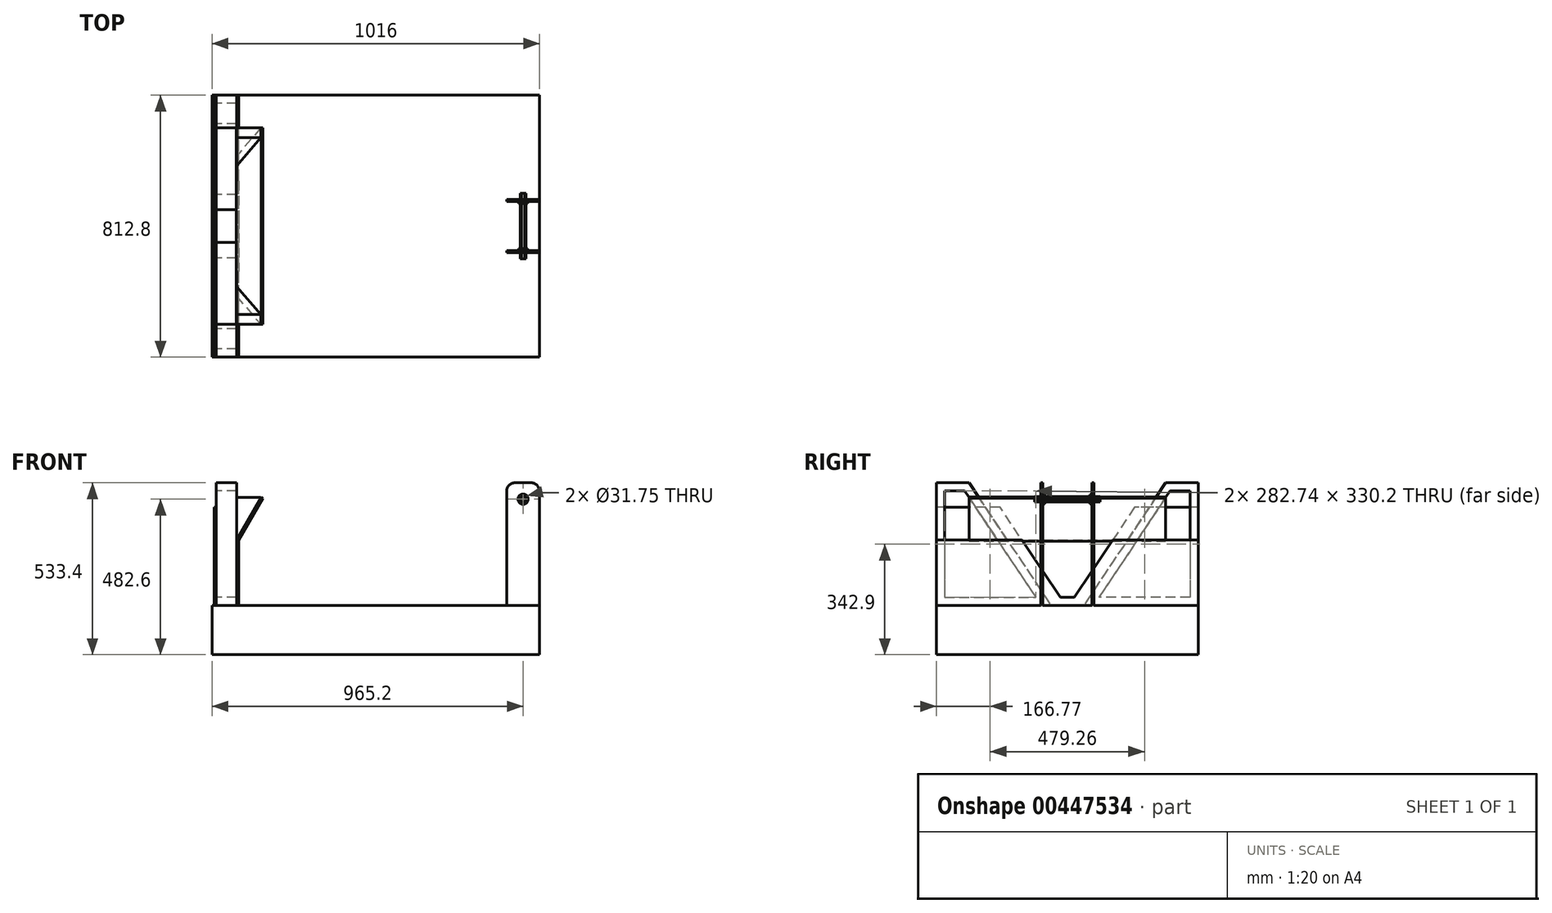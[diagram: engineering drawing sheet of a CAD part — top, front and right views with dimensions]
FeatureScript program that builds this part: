
annotation { "Feature Type Name" : "Feature", "Feature Type Description" : "" }
export const myFeature = defineFeature(function(context is Context, id is Id, definition is map)
    precondition{}
    {
        {
            var Q0;
            Q0=qCreatedBy(makeId("Top.planeOp"),FACE);
            cPlane(context, id + "F0", {"entities" : qUnion([Q0]), "cplaneType" : CPlaneType.OFFSET, "offset" : 76.2 * mm, "width" : 152.4 * mm, "height" : 152.4 * mm});
        }
        {
            var Q0;
            Q0=qCreatedBy(id+"F0.planeOp",FACE);
            var sketch = newSketch(context, id + "F1", { "sketchPlane" : qUnion([Q0])});
            skLineSegment(sketch, "E0.bottom", {"start": v(508, -406.4) * mm, "end": v(-508, -406.4) * mm});
            skLineSegment(sketch, "E0.top", {"start": v(508, 406.4) * mm, "end": v(-508, 406.4) * mm});
            skLineSegment(sketch, "E0.left", {"start": v(508, -406.4) * mm, "end": v(508, 406.4) * mm});
            skLineSegment(sketch, "E0.right", {"start": v(-508, -406.4) * mm, "end": v(-508, 406.4) * mm});
            skPoint(sketch, "E0.middle", {"position": v(0, 0) * mm});
            skSolve(sketch);
        }
        {
            var Q0;
            Q0 = qSketchRegion(id + "F1", true);
            extrude(context, id + "F2", {"entities" : qUnion([Q0]), "depth" : 152.4 * mm});
        }
        {
            var Q0;
            Q0=makeQuery(id+"F2.opExtrude","SWEPT_FACE",FACE,{"disambiguationData":[OSD([sQuery(id+"F1.wireOp",EDGE,"E0.right")])]});
            cPlane(context, id + "F3", {"entities" : qUnion([Q0]), "cplaneType" : CPlaneType.OFFSET, "offset" : 12.7 * mm, "oppositeDirection" : true, "width" : 152.4 * mm, "height" : 152.4 * mm});
        }
        {
            var Q0;
            Q0=qCreatedBy(id+"F3.planeOp",FACE);
            var sketch = newSketch(context, id + "F4", { "sketchPlane" : qUnion([Q0])});
            skLineSegment(sketch, "E1", {"start": v(-406.4, 609.6) * mm, "end": v(-406.4, 228.6) * mm});
            skLineSegment(sketch, "E2", {"start": v(-406.4, 228.6) * mm, "end": v(-50.8, 228.6) * mm});
            skLineSegment(sketch, "E3", {"start": v(0, 0) * mm, "end": v(-770.92, 0) * mm, "construction": true});
            skLineSegment(sketch, "E4", {"start": v(0, 0) * mm, "end": v(0, 808.5) * mm, "construction": true});
            skPoint(sketch, "E4.endSnap0", {"position": v(0, 228.6) * mm});
            skCircle(sketch, "E5", {"center": v(0, 404.25) * mm, "radius": 139.7 * mm, "construction": true});
            skLineSegment(sketch, "E6", {"start": v(-406.4, 609.6) * mm, "end": v(-304.8, 609.6) * mm});
            skLineSegment(sketch, "E7", {"start": v(-304.8, 609.6) * mm, "end": v(-50.8, 228.6) * mm});
            skLineSegment(sketch, "E8", {"start": v(-527.33, 330.2) * mm, "end": v(421.98, 330.2) * mm, "construction": true});
            skCircle(sketch, "E9", {"center": v(0, 404.25) * mm, "radius": 9.52 * mm, "construction": true});
            skLineSegment(sketch, "E10.MirrorCS", {"start": v(304.8, 609.6) * mm, "end": v(50.8, 228.6) * mm});
            skLineSegment(sketch, "E11.MirrorCS", {"start": v(406.4, 609.6) * mm, "end": v(304.8, 609.6) * mm});
            skLineSegment(sketch, "E12.MirrorCS", {"start": v(406.4, 609.6) * mm, "end": v(406.4, 228.6) * mm});
            skLineSegment(sketch, "E13.MirrorCS", {"start": v(406.4, 228.6) * mm, "end": v(50.8, 228.6) * mm});
            skLineSegment(sketch, "E14.0", {"start": v(-318.4, 584.2) * mm, "end": v(-98.26, 254) * mm});
            skLineSegment(sketch, "E14.1", {"start": v(-381, 584.2) * mm, "end": v(-318.4, 584.2) * mm});
            skLineSegment(sketch, "E14.2", {"start": v(-381, 584.2) * mm, "end": v(-381, 254) * mm});
            skLineSegment(sketch, "E14.3", {"start": v(-381, 254) * mm, "end": v(-98.26, 254) * mm});
            skLineSegment(sketch, "E15.0", {"start": v(318.4, 584.2) * mm, "end": v(98.26, 254) * mm});
            skLineSegment(sketch, "E15.1", {"start": v(381, 584.2) * mm, "end": v(318.4, 584.2) * mm});
            skLineSegment(sketch, "E15.2", {"start": v(381, 584.2) * mm, "end": v(381, 254) * mm});
            skLineSegment(sketch, "E15.3", {"start": v(381, 254) * mm, "end": v(98.26, 254) * mm});
            skSolve(sketch);
        }
        {
            var Q0;
            Q0=makeQuery(id+"F4.imprint","IMPRINT",FACE,{"disambiguationData":[TD([[makeQuery(id+"F4.imprint","IMPRINT",EDGE,{"derivedFrom":sQuery(id+"F4.wireOp",EDGE,"E1")}),1.0]])]});
            var Q1;
            Q1=makeQuery(id+"F4.imprint","IMPRINT",FACE,{"disambiguationData":[TD([[makeQuery(id+"F4.imprint","IMPRINT",EDGE,{"derivedFrom":sQuery(id+"F4.wireOp",EDGE,"E10.MirrorCS")}),1.0]])]});
            extrude(context, id + "F5", {"entities" : qUnion([Q0, Q1]), "oppositeDirection" : true, "depth" : 63.5 * mm});
        }
        {
            var Q0;
            Q0=makeQuery(id+"F5.opExtrude","CAP_FACE",FACE,{"disambiguationData":[OSD([sQuery(id+"F4.wireOp",EDGE,"E1"),sQuery(id+"F4.wireOp",EDGE,"E2"),sQuery(id+"F4.wireOp",EDGE,"E6"),sQuery(id+"F4.wireOp",EDGE,"E7"),sQuery(id+"F4.wireOp",EDGE,"E14.0"),sQuery(id+"F4.wireOp",EDGE,"E14.1"),sQuery(id+"F4.wireOp",EDGE,"E14.2"),sQuery(id+"F4.wireOp",EDGE,"E14.3")])],"isStart":true});
            var sketch = newSketch(context, id + "F6", { "sketchPlane" : qUnion([Q0])});
            skLineSegment(sketch, "E16.0", {"start": v(-406.4, 533.4) * mm, "end": v(-406.4, 228.6) * mm});
            skLineSegment(sketch, "E17.0", {"start": v(406.4, 533.4) * mm, "end": v(406.4, 228.6) * mm});
            skLineSegment(sketch, "E18", {"start": v(-406.4, 533.4) * mm, "end": v(-208.2, 533.4) * mm});
            skLineSegment(sketch, "E19", {"start": v(-208.2, 533.4) * mm, "end": v(-21.94, 254) * mm});
            skLineSegment(sketch, "E20", {"start": v(-21.94, 254) * mm, "end": v(21.94, 254) * mm});
            skLineSegment(sketch, "E21", {"start": v(21.94, 254) * mm, "end": v(208.2, 533.4) * mm});
            skLineSegment(sketch, "E22", {"start": v(208.2, 533.4) * mm, "end": v(406.4, 533.4) * mm});
            skLineSegment(sketch, "E23", {"start": v(-406.4, 228.6) * mm, "end": v(406.4, 228.6) * mm});
            skPoint(sketch, "E24.orphan", {"position": v(-406.4, 609.6) * mm});
            skPoint(sketch, "E25.orphan", {"position": v(406.4, 609.6) * mm});
            skSolve(sketch);
        }
        {
            var Q0;
            Q0 = qSketchRegion(id + "F6", true);
            extrude(context, id + "F7", {"entities" : qUnion([Q0]), "depth" : 6.35 * mm});
        }
        {
            var Q0;
            Q0=makeQuery(id+"F5.opExtrude","CAP_FACE",FACE,{"disambiguationData":[OSD([sQuery(id+"F4.wireOp",EDGE,"E1"),sQuery(id+"F4.wireOp",EDGE,"E2"),sQuery(id+"F4.wireOp",EDGE,"E6"),sQuery(id+"F4.wireOp",EDGE,"E7"),sQuery(id+"F4.wireOp",EDGE,"E14.0"),sQuery(id+"F4.wireOp",EDGE,"E14.1"),sQuery(id+"F4.wireOp",EDGE,"E14.2"),sQuery(id+"F4.wireOp",EDGE,"E14.3")])],"isStart":false});
            var sketch = newSketch(context, id + "F8", { "sketchPlane" : qUnion([Q0])});
            skLineSegment(sketch, "E26.0", {"start": v(-21.94, 254) * mm, "end": v(-140.48, 431.8) * mm});
            skLineSegment(sketch, "E27.0", {"start": v(140.48, 431.8) * mm, "end": v(21.94, 254) * mm});
            skLineSegment(sketch, "E28.0", {"start": v(406.4, 431.8) * mm, "end": v(406.4, 228.6) * mm});
            skLineSegment(sketch, "E29.0", {"start": v(-406.4, 228.6) * mm, "end": v(406.4, 228.6) * mm});
            skLineSegment(sketch, "E30.0", {"start": v(-406.4, 431.8) * mm, "end": v(-406.4, 228.6) * mm});
            skPoint(sketch, "E31.orphan", {"position": v(-406.4, 609.6) * mm});
            skPoint(sketch, "E32.orphan", {"position": v(406.4, 609.6) * mm});
            skLineSegment(sketch, "E33.0", {"start": v(21.94, 254) * mm, "end": v(-21.94, 254) * mm});
            skLineSegment(sketch, "E34", {"start": v(-406.4, 431.8) * mm, "end": v(-140.48, 431.8) * mm});
            skLineSegment(sketch, "E35.trimOffspring", {"start": v(140.48, 431.8) * mm, "end": v(406.4, 431.8) * mm});
            skPoint(sketch, "E36.0.start.orphan", {"position": v(-208.2, 533.4) * mm});
            skPoint(sketch, "E37.0.end.orphan", {"position": v(208.2, 533.4) * mm});
            skPoint(sketch, "E38.orphan", {"position": v(406.4, 533.4) * mm});
            skPoint(sketch, "E39.orphan", {"position": v(-406.4, 533.4) * mm});
            skSolve(sketch);
        }
        {
            var Q0;
            Q0 = qSketchRegion(id + "F8", true);
            extrude(context, id + "F9", {"entities" : qUnion([Q0]), "depth" : 6.35 * mm});
        }
        {
            var Q0;
            Q0=makeQuery(id+"F9.opExtrude","CAP_EDGE",EDGE,{"disambiguationData":[OSD([sQuery(id+"F8.wireOp",EDGE,"E35.trimOffspring")])],"isStart":false});
            var Q1;
            Q1=makeQuery(id+"F5.opExtrude","CAP_FACE",FACE,{"disambiguationData":[OSD([sQuery(id+"F4.wireOp",EDGE,"E1"),sQuery(id+"F4.wireOp",EDGE,"E2"),sQuery(id+"F4.wireOp",EDGE,"E6"),sQuery(id+"F4.wireOp",EDGE,"E7"),sQuery(id+"F4.wireOp",EDGE,"E14.0"),sQuery(id+"F4.wireOp",EDGE,"E14.1"),sQuery(id+"F4.wireOp",EDGE,"E14.2"),sQuery(id+"F4.wireOp",EDGE,"E14.3")])],"isStart":false});
            cPlane(context, id + "F10", {"entities" : qUnion([Q0, Q1]), "cplaneType" : CPlaneType.LINE_ANGLE, "offset" : 25.4 * mm, "angle" : 30 * degree, "width" : 152.4 * mm, "height" : 152.4 * mm});
        }
        {
            var Q0;
            Q0=qCreatedBy(id+"F10.planeOp",FACE);
            var sketch = newSketch(context, id + "F11", { "sketchPlane" : qUnion([Q0])});
            skLineSegment(sketch, "E40.bottom", {"start": v(304.8, 312.03) * mm, "end": v(-304.8, 312.03) * mm});
            skLineSegment(sketch, "E40.top", {"start": v(304.8, 158.05) * mm, "end": v(-304.8, 158.05) * mm});
            skLineSegment(sketch, "E40.left", {"start": v(304.8, 312.03) * mm, "end": v(304.8, 158.05) * mm});
            skLineSegment(sketch, "E40.right", {"start": v(-304.8, 312.03) * mm, "end": v(-304.8, 158.05) * mm});
            skSolve(sketch);
        }
        {
            var Q0;
            Q0=makeQuery(id+"F11.imprint","IMPRINT",FACE,{"disambiguationData":[TD([[makeQuery(id+"F11.imprint","IMPRINT",EDGE,{"derivedFrom":sQuery(id+"F11.wireOp",EDGE,"E40.bottom")}),1.0]])]});
            extrude(context, id + "F12", {"entities" : qUnion([Q0]), "depth" : 6.35 * mm});
        }
        {
            var Q0;
            Q0=makeQuery(id+"F5.opExtrude","CAP_FACE",FACE,{"disambiguationData":[OSD([sQuery(id+"F4.wireOp",EDGE,"E10.MirrorCS"),sQuery(id+"F4.wireOp",EDGE,"E11.MirrorCS"),sQuery(id+"F4.wireOp",EDGE,"E12.MirrorCS"),sQuery(id+"F4.wireOp",EDGE,"E13.MirrorCS"),sQuery(id+"F4.wireOp",EDGE,"E15.0"),sQuery(id+"F4.wireOp",EDGE,"E15.1"),sQuery(id+"F4.wireOp",EDGE,"E15.2"),sQuery(id+"F4.wireOp",EDGE,"E15.3")])],"isStart":false});
            var sketch = newSketch(context, id + "F13", { "sketchPlane" : qUnion([Q0])});
            skLineSegment(sketch, "E41", {"start": v(-304.8, 563.82) * mm, "end": v(-274.28, 563.82) * mm});
            skLineSegment(sketch, "E42", {"start": v(-274.28, 563.82) * mm, "end": v(-186.5, 432.15) * mm});
            skLineSegment(sketch, "E43", {"start": v(-186.5, 432.15) * mm, "end": v(-217.02, 432.15) * mm});
            skLineSegment(sketch, "E44", {"start": v(-217.02, 432.15) * mm, "end": v(-304.8, 563.82) * mm});
            skLineSegment(sketch, "E45.MirrorCS", {"start": v(274.28, 563.82) * mm, "end": v(186.5, 432.15) * mm});
            skLineSegment(sketch, "E46.MirrorCS", {"start": v(217.02, 432.15) * mm, "end": v(304.8, 563.82) * mm});
            skLineSegment(sketch, "E47.MirrorCS", {"start": v(186.5, 432.15) * mm, "end": v(217.02, 432.15) * mm});
            skLineSegment(sketch, "E48.MirrorCS", {"start": v(304.8, 563.82) * mm, "end": v(274.28, 563.82) * mm});
            skSolve(sketch);
        }
        {
            var Q0;
            Q0 = qSketchRegion(id + "F13", true);
            var Q1;
            Q1=makeQuery(id+"F12.opExtrude","CAP_FACE",FACE,{"disambiguationData":[OSD([sQuery(id+"F11.wireOp",EDGE,"E40.bottom"),sQuery(id+"F11.wireOp",EDGE,"E40.top"),sQuery(id+"F11.wireOp",EDGE,"E40.left"),sQuery(id+"F11.wireOp",EDGE,"E40.right")])],"isStart":false});
            extrude(context, id + "F14", {"entities" : qUnion([Q0]), "endBound" : BoundingType.UP_TO_SURFACE, "endBoundEntityFace" : qUnion([Q1]), "depth" : 25.4 * mm});
        }
        {
            var Q0;
            Q0=makeQuery(id+"F2.opExtrude","SWEPT_FACE",FACE,{"disambiguationData":[OSD([sQuery(id+"F1.wireOp",EDGE,"E0.left")])]});
            var sketch = newSketch(context, id + "F15", { "sketchPlane" : qUnion([Q0])});
            skLineSegment(sketch, "E49.bottom", {"start": v(-76.2, 228.6) * mm, "end": v(-82.55, 228.6) * mm});
            skLineSegment(sketch, "E49.top", {"start": v(-76.2, 609.6) * mm, "end": v(-82.55, 609.6) * mm});
            skLineSegment(sketch, "E49.left", {"start": v(-76.2, 228.6) * mm, "end": v(-76.2, 609.6) * mm});
            skLineSegment(sketch, "E49.right", {"start": v(-82.55, 228.6) * mm, "end": v(-82.55, 609.6) * mm});
            skLineSegment(sketch, "E50.MirrorCS", {"start": v(76.2, 228.6) * mm, "end": v(76.2, 609.6) * mm});
            skLineSegment(sketch, "E51.MirrorCS", {"start": v(82.55, 228.6) * mm, "end": v(82.55, 609.6) * mm});
            skLineSegment(sketch, "E52.MirrorCS", {"start": v(76.2, 609.6) * mm, "end": v(82.55, 609.6) * mm});
            skLineSegment(sketch, "E53.MirrorCS", {"start": v(76.2, 228.6) * mm, "end": v(82.55, 228.6) * mm});
            skSolve(sketch);
        }
        {
            var Q0;
            Q0 = qSketchRegion(id + "F15", true);
            extrude(context, id + "F16", {"entities" : qUnion([Q0]), "operationType" : NewBodyOperationType.ADD, "oppositeDirection" : true, "depth" : 101.6 * mm});
        }
        {
            var Q0;
            Q0=makeQuery(id+"F16.opExtrude","SWEPT_FACE",FACE,{"disambiguationData":[OSD([sQuery(id+"F15.wireOp",EDGE,"E49.right")])]});
            var sketch = newSketch(context, id + "F17", { "sketchPlane" : qUnion([Q0])});
            skCircle(sketch, "E54", {"center": v(457.2, 558.8) * mm, "radius": 15.88 * mm});
            skPoint(sketch, "E54.centerSnap0", {"position": v(457.2, 609.6) * mm});
            skSolve(sketch);
        }
        {
            var Q0;
            Q0 = qSketchRegion(id + "F17", true);
            extrude(context, id + "F18", {"entities" : qUnion([Q0]), "operationType" : NewBodyOperationType.REMOVE, "endBound" : BoundingType.THROUGH_ALL, "oppositeDirection" : true, "depth" : 25.4 * mm});
        }
        {
            var Q0;
            Q0=makeQuery(id+"F16.opExtrude","CAP_EDGE",EDGE,{"disambiguationData":[OSD([sQuery(id+"F15.wireOp",EDGE,"E49.top")])],"isStart":true});
            var Q1;
            Q1=makeQuery(id+"F16.opExtrude","CAP_EDGE",EDGE,{"disambiguationData":[OSD([sQuery(id+"F15.wireOp",EDGE,"E49.top")])],"isStart":false});
            var Q2;
            Q2=makeQuery(id+"F16.opExtrude","CAP_EDGE",EDGE,{"disambiguationData":[OSD([sQuery(id+"F15.wireOp",EDGE,"E52.MirrorCS")])],"isStart":true});
            var Q3;
            Q3=makeQuery(id+"F16.opExtrude","CAP_EDGE",EDGE,{"disambiguationData":[OSD([sQuery(id+"F15.wireOp",EDGE,"E52.MirrorCS")])],"isStart":false});
            fillet(context, id + "F19", {"entities" : qUnion([Q0, Q1, Q2, Q3]), "radius" : 25.4 * mm, "tangentPropagation" : true, "allowEdgeOverflow" : false});
        }
        {
            var Q0;
            Q0=makeQuery(id+"F16.opExtrude","SWEPT_FACE",FACE,{"disambiguationData":[OSD([sQuery(id+"F15.wireOp",EDGE,"E49.right")])]});
            var sketch = newSketch(context, id + "F20", { "sketchPlane" : qUnion([Q0])});
            skCircle(sketch, "E55", {"center": v(457.2, 558.8) * mm, "radius": 14.29 * mm});
            skCircle(sketch, "E56.cCircle", {"center": v(457.2, 558.8) * mm, "radius": 7.94 * mm, "construction": true});
            skLineSegment(sketch, "E56.0", {"start": v(452.62, 566.74) * mm, "end": v(461.78, 566.74) * mm});
            skLineSegment(sketch, "E56.1", {"start": v(461.78, 566.74) * mm, "end": v(466.37, 558.8) * mm});
            skLineSegment(sketch, "E56.2", {"start": v(466.37, 558.8) * mm, "end": v(461.78, 550.86) * mm});
            skLineSegment(sketch, "E56.3", {"start": v(461.78, 550.86) * mm, "end": v(452.62, 550.86) * mm});
            skLineSegment(sketch, "E56.4", {"start": v(452.62, 550.86) * mm, "end": v(448.03, 558.8) * mm});
            skLineSegment(sketch, "E56.5", {"start": v(448.03, 558.8) * mm, "end": v(452.62, 566.74) * mm});
            skPoint(sketch, "E56.0.midPoint", {"position": v(457.2, 566.74) * mm});
            skSolve(sketch);
        }
        {
            var Q0;
            Q0=makeQuery(id+"F20.imprint","IMPRINT",FACE,{"disambiguationData":[TD([[makeQuery(id+"F20.imprint","IMPRINT",EDGE,{"derivedFrom":sQuery(id+"F20.wireOp",EDGE,"E55")}),1.0]])]});
            extrude(context, id + "F21", {"entities" : qUnion([Q0]), "oppositeDirection" : true, "depth" : 12.7 * mm});
        }
        {
            var Q0;
            Q0=makeQuery(id+"F21.opExtrude","SWEPT_BODY",BODY,{"disambiguationData":[OSD([sQuery(id+"F20.wireOp",EDGE,"E55"),sQuery(id+"F20.wireOp",EDGE,"E56.0"),sQuery(id+"F20.wireOp",EDGE,"E56.1"),sQuery(id+"F20.wireOp",EDGE,"E56.2"),sQuery(id+"F20.wireOp",EDGE,"E56.3"),sQuery(id+"F20.wireOp",EDGE,"E56.4"),sQuery(id+"F20.wireOp",EDGE,"E56.5")])]});
            var Q1;
            Q1=qCreatedBy(makeId("Front.planeOp"),FACE);
            mirror(context, id + "F22", {"entities" : qUnion([Q0]), "mirrorPlane" : qUnion([Q1])});
        }
        {
            var Q0;
            Q0=qCreatedBy(makeId("Front.planeOp"),FACE);
            var sketch = newSketch(context, id + "F23", { "sketchPlane" : qUnion([Q0])});
            skLineSegment(sketch, "E57.0", {"start": v(448.03, 558.8) * mm, "end": v(452.62, 566.74) * mm});
            skLineSegment(sketch, "E58.0", {"start": v(452.62, 550.86) * mm, "end": v(448.03, 558.8) * mm});
            skLineSegment(sketch, "E59.0", {"start": v(461.78, 550.86) * mm, "end": v(452.62, 550.86) * mm});
            skLineSegment(sketch, "E60.0", {"start": v(466.37, 558.8) * mm, "end": v(461.78, 550.86) * mm});
            skLineSegment(sketch, "E61.0", {"start": v(461.78, 566.74) * mm, "end": v(466.37, 558.8) * mm});
            skLineSegment(sketch, "E62.0", {"start": v(452.62, 566.74) * mm, "end": v(461.78, 566.74) * mm});
            skSolve(sketch);
        }
        {
            var Q0;
            Q0=makeQuery(id+"F23.imprint","IMPRINT",FACE,{"disambiguationData":[TD([[makeQuery(id+"F23.imprint","IMPRINT",EDGE,{"derivedFrom":sQuery(id+"F23.wireOp",EDGE,"E57.0")}),-1.0]])]});
            extrude(context, id + "F24", {"entities" : qUnion([Q0]), "endBound" : BoundingType.SYMMETRIC, "depth" : 203.2 * mm});
        }
    });
